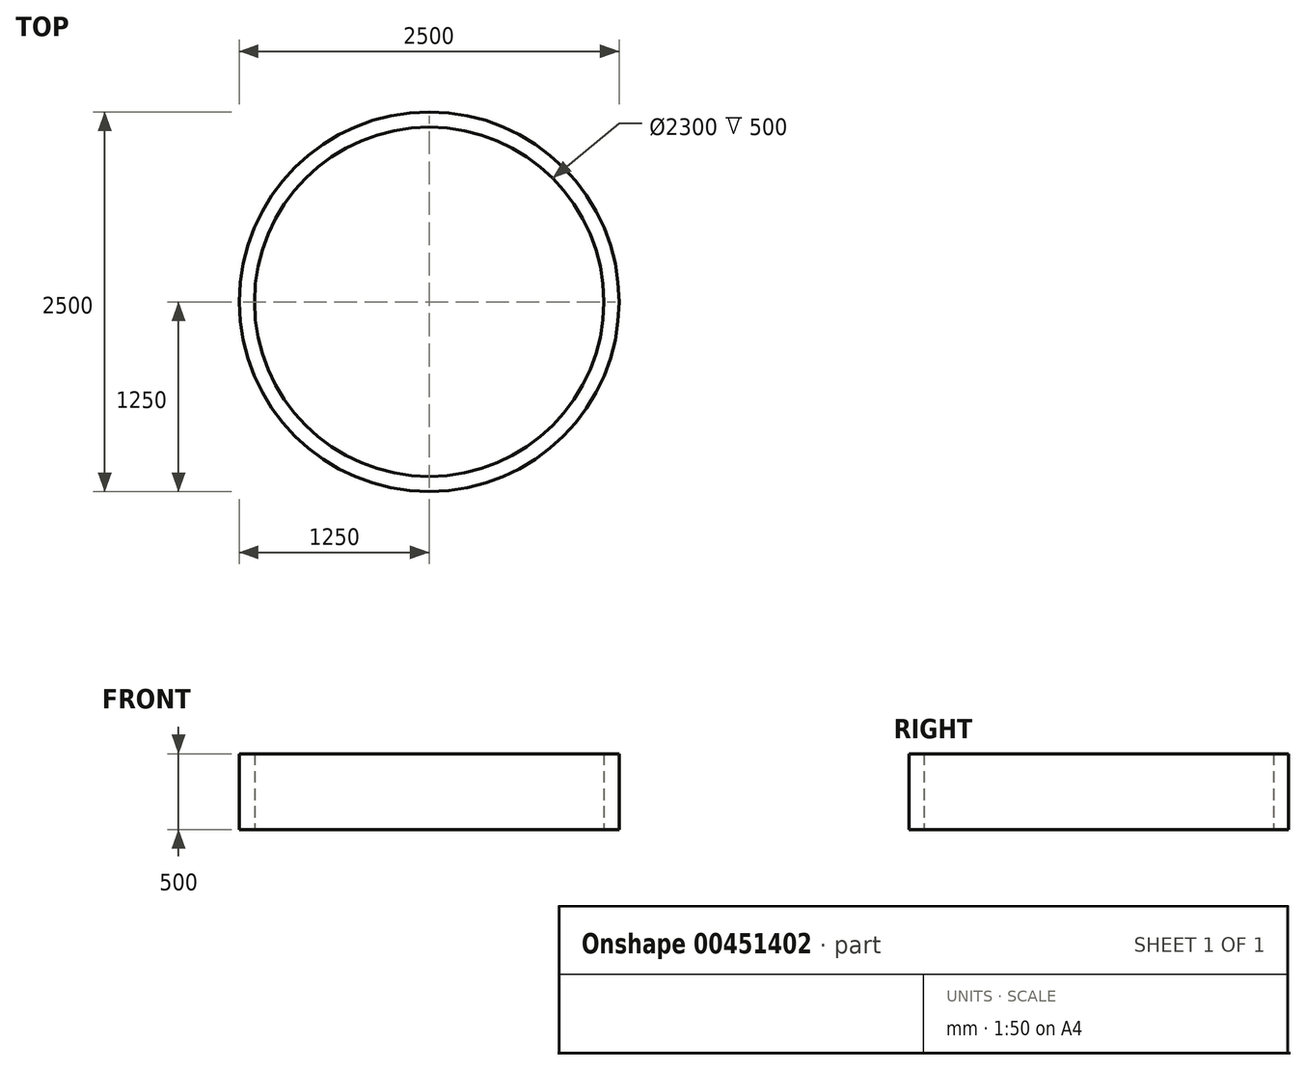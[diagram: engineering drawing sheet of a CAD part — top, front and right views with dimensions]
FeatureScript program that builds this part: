
annotation { "Feature Type Name" : "Feature", "Feature Type Description" : "" }
export const myFeature = defineFeature(function(context is Context, id is Id, definition is map)
    precondition{}
    {
        {
            var Q0;
            Q0=qCreatedBy(makeId("Top.planeOp"),FACE);
            var sketch = newSketch(context, id + "F0", { "sketchPlane" : qUnion([Q0])});
            skCircle(sketch, "E0", {"center": v(0, 0) * mm, "radius": 1250 * mm});
            skCircle(sketch, "E1", {"center": v(0, 0) * mm, "radius": 1150 * mm});
            skSolve(sketch);
        }
        {
            var Q0;
            Q0=makeQuery(id+"F0.imprint","IMPRINT",FACE,{"disambiguationData":[TD([[makeQuery(id+"F0.imprint","IMPRINT",EDGE,{"derivedFrom":sQuery(id+"F0.wireOp",EDGE,"E0")}),1.0]])]});
            extrude(context, id + "F1", {"entities" : qUnion([Q0]), "endBound" : BoundingType.SYMMETRIC, "depth" : 500 * mm});
        }
    });
